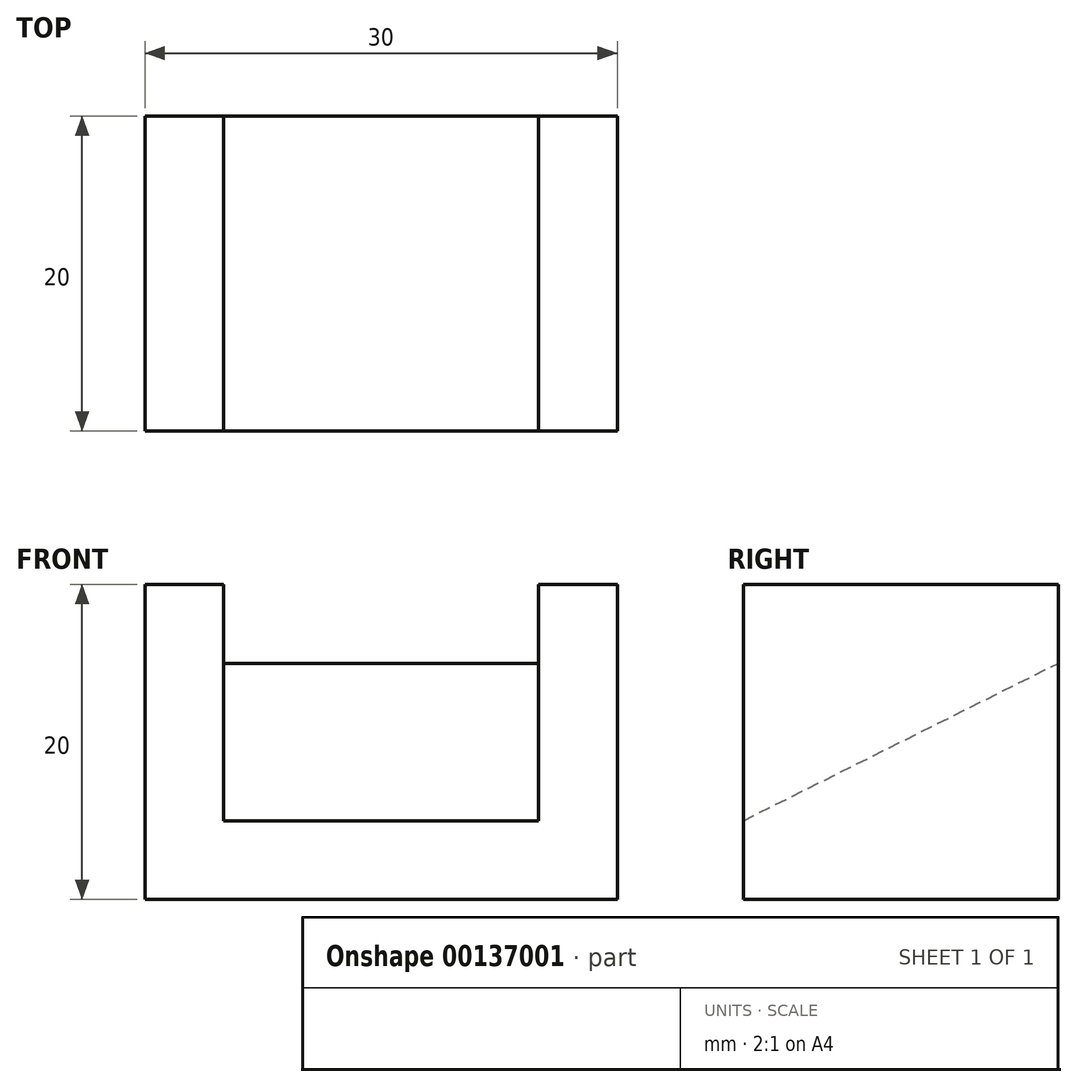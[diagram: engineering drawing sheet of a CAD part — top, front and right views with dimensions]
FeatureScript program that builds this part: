
annotation { "Feature Type Name" : "Feature", "Feature Type Description" : "" }
export const myFeature = defineFeature(function(context is Context, id is Id, definition is map)
    precondition{}
    {
        {
            var Q0;
            Q0=qCreatedBy(makeId("Right.planeOp"),FACE);
            var sketch = newSketch(context, id + "F0", { "sketchPlane" : qUnion([Q0])});
            skLineSegment(sketch, "E0.bottom", {"start": v(0, 0) * mm, "end": v(-20, 0) * mm});
            skLineSegment(sketch, "E0.top", {"start": v(0, 20) * mm, "end": v(-20, 20) * mm});
            skLineSegment(sketch, "E0.left", {"start": v(0, 0) * mm, "end": v(0, 20) * mm});
            skLineSegment(sketch, "E0.right", {"start": v(-20, 0) * mm, "end": v(-20, 20) * mm});
            skSolve(sketch);
        }
        {
            var Q0;
            Q0 = qSketchRegion(id + "F0", true);
            extrude(context, id + "F1", {"entities" : qUnion([Q0]), "depth" : 5 * mm});
        }
        {
            var Q0;
            Q0=makeQuery(id+"F1.opExtrude","CAP_FACE",FACE,{"disambiguationData":[OSD([sQuery(id+"F0.wireOp",EDGE,"E0.bottom"),sQuery(id+"F0.wireOp",EDGE,"E0.top"),sQuery(id+"F0.wireOp",EDGE,"E0.left"),sQuery(id+"F0.wireOp",EDGE,"E0.right")])],"isStart":false});
            var sketch = newSketch(context, id + "F2", { "sketchPlane" : qUnion([Q0])});
            skLineSegment(sketch, "E1", {"start": v(-20, 0) * mm, "end": v(-20, 5) * mm});
            skLineSegment(sketch, "E2", {"start": v(-20, 5) * mm, "end": v(0, 15) * mm});
            skLineSegment(sketch, "E3", {"start": v(0, 15) * mm, "end": v(0, 0) * mm});
            skLineSegment(sketch, "E4", {"start": v(0, 0) * mm, "end": v(-20, 0) * mm});
            skSolve(sketch);
        }
        {
            var Q0;
            Q0 = qSketchRegion(id + "F2", true);
            extrude(context, id + "F3", {"entities" : qUnion([Q0]), "operationType" : NewBodyOperationType.ADD, "depth" : 20 * mm});
        }
        {
            var Q0;
            Q0=makeQuery(id+"F3.opExtrude","CAP_FACE",FACE,{"disambiguationData":[OSD([sQuery(id+"F2.wireOp",EDGE,"E1"),sQuery(id+"F2.wireOp",EDGE,"E2"),sQuery(id+"F2.wireOp",EDGE,"E3"),sQuery(id+"F2.wireOp",EDGE,"E4")])],"isStart":false});
            var sketch = newSketch(context, id + "F4", { "sketchPlane" : qUnion([Q0])});
            skLineSegment(sketch, "E5.bottom", {"start": v(0, 0) * mm, "end": v(-20, 0) * mm});
            skLineSegment(sketch, "E5.top", {"start": v(0, 20) * mm, "end": v(-20, 20) * mm});
            skLineSegment(sketch, "E5.left", {"start": v(0, 0) * mm, "end": v(0, 20) * mm});
            skLineSegment(sketch, "E5.right", {"start": v(-20, 0) * mm, "end": v(-20, 20) * mm});
            skSolve(sketch);
        }
        {
            var Q0;
            Q0 = qSketchRegion(id + "F4", true);
            extrude(context, id + "F5", {"entities" : qUnion([Q0]), "operationType" : NewBodyOperationType.ADD, "depth" : 5 * mm});
        }
    });
